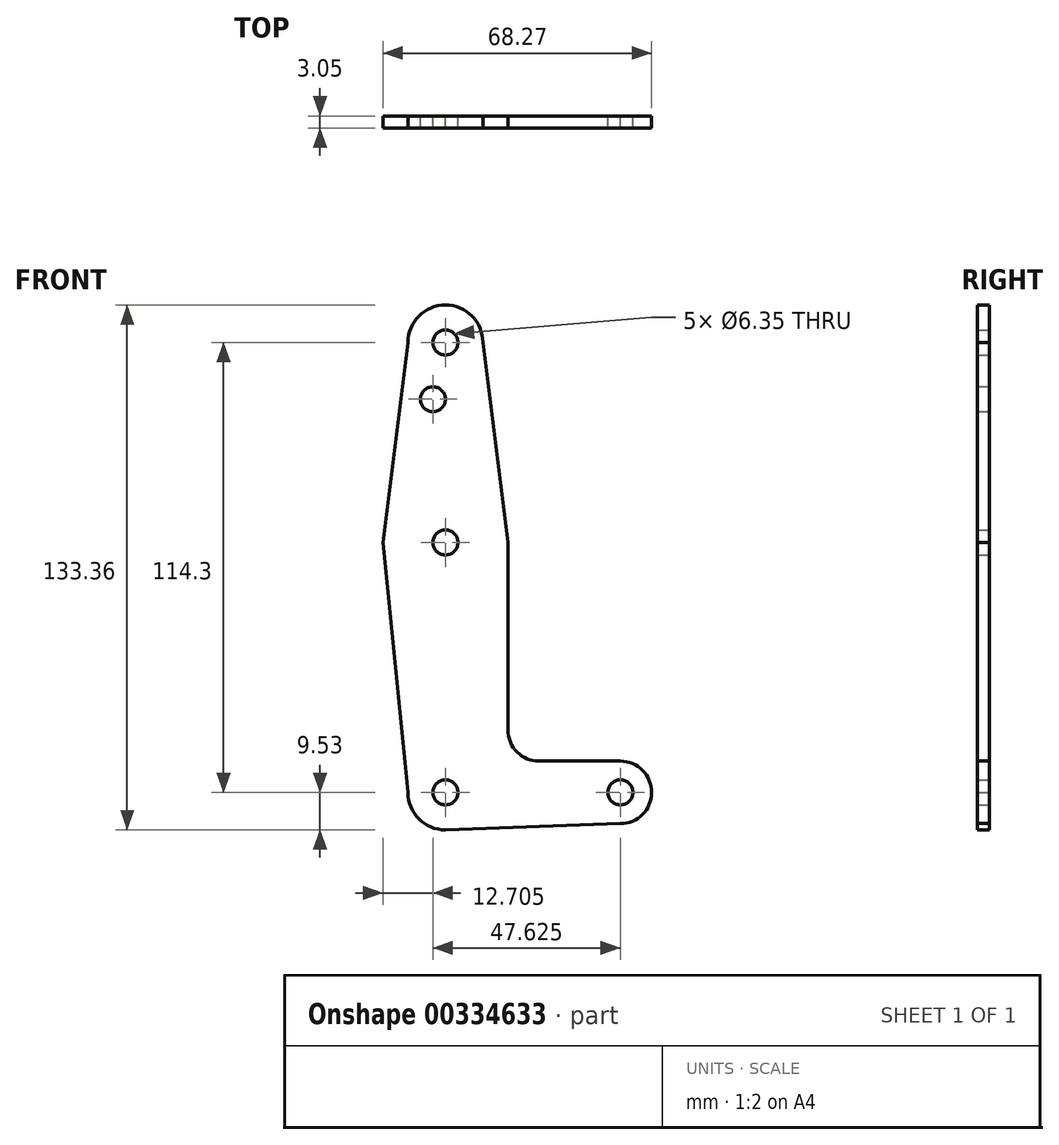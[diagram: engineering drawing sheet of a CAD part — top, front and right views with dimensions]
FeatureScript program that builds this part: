
annotation { "Feature Type Name" : "Feature", "Feature Type Description" : "" }
export const myFeature = defineFeature(function(context is Context, id is Id, definition is map)
    precondition{}
    {
        {
            var Q0;
            Q0=qCreatedBy(makeId("Front.planeOp"),FACE);
            var sketch = newSketch(context, id + "F0", { "sketchPlane" : qUnion([Q0])});
            skLineSegment(sketch, "E0", {"start": v(0, 0) * mm, "end": v(0, 114.3) * mm});
            skLineSegment(sketch, "E1", {"start": v(0, 0) * mm, "end": v(44.45, 0) * mm});
            skCircle(sketch, "E2", {"center": v(44.45, 0) * mm, "radius": 7.94 * mm});
            skCircle(sketch, "E3", {"center": v(0, 114.3) * mm, "radius": 9.53 * mm});
            skCircle(sketch, "E4", {"center": v(0, 63.5) * mm, "radius": 15.88 * mm});
            skCircle(sketch, "E5", {"center": v(0, 0) * mm, "radius": 9.53 * mm});
            skLineSegment(sketch, "E6", {"start": v(-15.88, 63.5) * mm, "end": v(-9.52, 114.3) * mm});
            skLineSegment(sketch, "E7", {"start": v(-15.88, 63.5) * mm, "end": v(-9.52, 0) * mm});
            skLineSegment(sketch, "E8", {"start": v(15.88, 63.5) * mm, "end": v(9.52, 114.3) * mm});
            skLineSegment(sketch, "E9", {"start": v(15.87, 63.5) * mm, "end": v(15.88, 15.89) * mm});
            skLineSegment(sketch, "E10", {"start": v(23.83, 7.94) * mm, "end": v(44.45, 7.94) * mm});
            skLineSegment(sketch, "E11", {"start": v(0, -9.52) * mm, "end": v(44.45, -7.94) * mm});
            skCircle(sketch, "E12", {"center": v(0, 114.3) * mm, "radius": 3.18 * mm});
            skCircle(sketch, "E13", {"center": v(0, 63.5) * mm, "radius": 3.18 * mm});
            skCircle(sketch, "E14", {"center": v(0, 0) * mm, "radius": 3.18 * mm});
            skCircle(sketch, "E15", {"center": v(44.45, 0) * mm, "radius": 3.18 * mm});
            skCircle(sketch, "E16", {"center": v(-3.18, 99.89) * mm, "radius": 3.18 * mm});
            skArc(sketch, "E17.filletArc", {"start": v(15.88, 15.89) * mm, "mid": v(18.2, 10.27) * mm, "end": v(23.83, 7.94) * mm});
            skSolve(sketch);
        }
        {
            var Q0;
            {var subQ8=sQuery(id+"F0.wireOp",EDGE,"E16");Q0=makeQuery(id+"F0.imprint","IMPRINT",FACE,{"disambiguationData":[TD([[makeQuery(id+"F0.imprint","IMPRINT",EDGE,{"derivedFrom":subQ8}),-1.0]])]});}
            var Q1;
            {var subQ3=sQuery(id+"F0.wireOp",EDGE,"E0");var subQ5=makeQuery(id+"F0.imprint","INTERSECT",VERTEX,{"derivedFrom":[subQ3,sQuery(id+"F0.wireOp",EDGE,"E16")]});Q1=makeQuery(id+"F0.imprint","IMPRINT",FACE,{"disambiguationData":[TD([[makeQuery(id+"F0.imprint","IMPRINT",EDGE,{"disambiguationData":[TD([[subQ5,1.0]])],"derivedFrom":subQ3}),-1.0]])]});}
            var Q2;
            Q2=makeQuery(id+"F0.imprint","IMPRINT",FACE,{"disambiguationData":[TD([[makeQuery(id+"F0.imprint","IMPRINT",EDGE,{"derivedFrom":sQuery(id+"F0.wireOp",EDGE,"E12")}),-1.0]])]});
            var Q3;
            {var subQ1=sQuery(id+"F0.wireOp",EDGE,"E0");var subQ3=sQuery(id+"F0.wireOp",EDGE,"E4");var subQ7=makeQuery(id+"F0.imprint","INTERSECT",VERTEX,{"disambiguationData":[OD(0.0)],"derivedFrom":[subQ1,subQ3]});Q3=makeQuery(id+"F0.imprint","IMPRINT",FACE,{"disambiguationData":[TD([[makeQuery(id+"F0.imprint","IMPRINT",EDGE,{"disambiguationData":[TD([[subQ7,-1.0]])],"derivedFrom":subQ1}),-1.0]])]});}
            var Q4;
            {var subQ1=sQuery(id+"F0.wireOp",EDGE,"E4");var subQ3=sQuery(id+"F0.wireOp",EDGE,"E0");var subQ4=makeQuery(id+"F0.imprint","INTERSECT",VERTEX,{"disambiguationData":[OD(0.0)],"derivedFrom":[subQ3,subQ1]});Q4=makeQuery(id+"F0.imprint","IMPRINT",FACE,{"disambiguationData":[TD([[makeQuery(id+"F0.imprint","IMPRINT",EDGE,{"disambiguationData":[TD([[subQ4,-1.0]])],"derivedFrom":subQ3}),1.0]])]});}
            var Q5;
            {var subQ0=sQuery(id+"F0.wireOp",EDGE,"E5");var subQ1=sQuery(id+"F0.wireOp",EDGE,"E0");var subQ2=makeQuery(id+"F0.imprint","INTERSECT",VERTEX,{"derivedFrom":[subQ1,subQ0]});Q5=makeQuery(id+"F0.imprint","IMPRINT",FACE,{"disambiguationData":[TD([[makeQuery(id+"F0.imprint","IMPRINT",EDGE,{"disambiguationData":[TD([[subQ2,-1.0]])],"derivedFrom":subQ1}),1.0]])]});}
            var Q6;
            {var subQ0=sQuery(id+"F0.wireOp",EDGE,"E2");var subQ1=sQuery(id+"F0.wireOp",EDGE,"E1");var subQ2=makeQuery(id+"F0.imprint","INTERSECT",VERTEX,{"derivedFrom":[subQ1,subQ0]});Q6=makeQuery(id+"F0.imprint","IMPRINT",FACE,{"disambiguationData":[TD([[makeQuery(id+"F0.imprint","IMPRINT",EDGE,{"disambiguationData":[TD([[subQ2,1.0]])],"derivedFrom":subQ1}),-1.0]])]});}
            var Q7;
            {var subQ2=sQuery(id+"F0.wireOp",EDGE,"E0");var subQ4=sQuery(id+"F0.wireOp",EDGE,"E14");var subQ11=makeQuery(id+"F0.imprint","INTERSECT",VERTEX,{"derivedFrom":[subQ2,subQ4]});Q7=makeQuery(id+"F0.imprint","IMPRINT",FACE,{"disambiguationData":[TD([[makeQuery(id+"F0.imprint","IMPRINT",EDGE,{"disambiguationData":[TD([[subQ11,-1.0]])],"derivedFrom":subQ2}),1.0]])]});}
            var Q8;
            {var subQ0=sQuery(id+"F0.wireOp",EDGE,"E9");Q8=makeQuery(id+"F0.imprint","IMPRINT",FACE,{"disambiguationData":[TD([[makeQuery(id+"F0.imprint","IMPRINT",EDGE,{"derivedFrom":subQ0}),-1.0]])]});}
            var Q9;
            {var subQ0=sQuery(id+"F0.wireOp",EDGE,"E14");var subQ1=sQuery(id+"F0.wireOp",EDGE,"E0");var subQ2=makeQuery(id+"F0.imprint","INTERSECT",VERTEX,{"derivedFrom":[subQ1,subQ0]});Q9=makeQuery(id+"F0.imprint","IMPRINT",FACE,{"disambiguationData":[TD([[makeQuery(id+"F0.imprint","IMPRINT",EDGE,{"disambiguationData":[TD([[subQ2,-1.0]])],"derivedFrom":subQ1}),-1.0]])]});}
            var Q10;
            Q10=makeQuery(id+"F0.imprint","IMPRINT",FACE,{"disambiguationData":[TD([[makeQuery(id+"F0.imprint","IMPRINT",EDGE,{"derivedFrom":sQuery(id+"F0.wireOp",EDGE,"E15")}),-1.0]])]});
            extrude(context, id + "F1", {"entities" : qUnion([Q0, Q1, Q2, Q3, Q4, Q5, Q6, Q7, Q8, Q9, Q10]), "depth" : 3.05 * mm});
        }
    });
